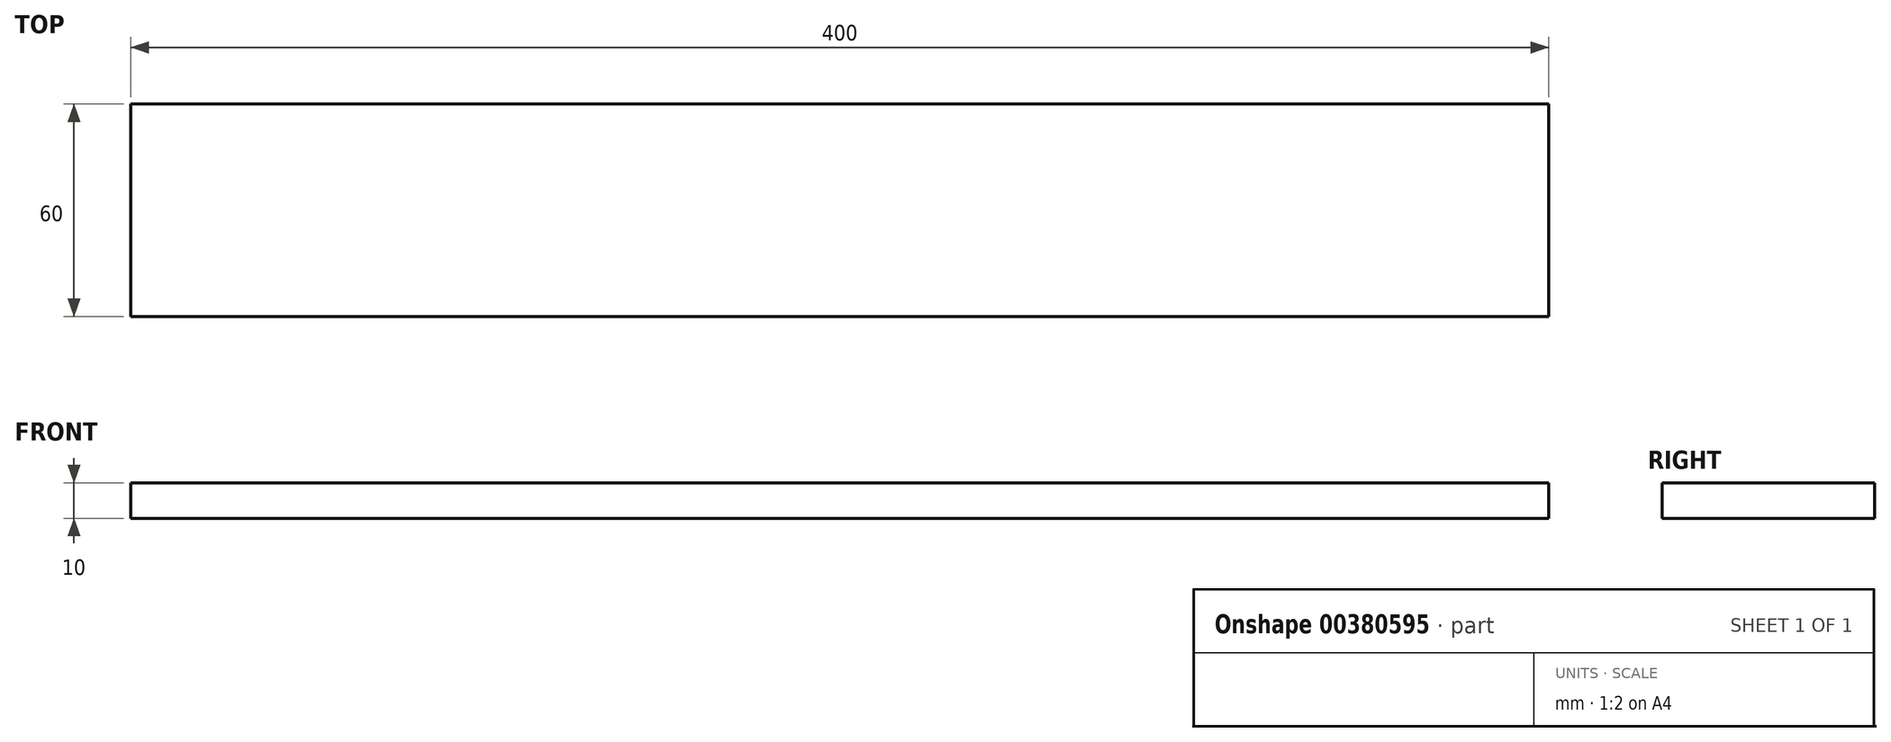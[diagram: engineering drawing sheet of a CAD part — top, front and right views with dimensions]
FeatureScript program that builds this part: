
annotation { "Feature Type Name" : "Feature", "Feature Type Description" : "" }
export const myFeature = defineFeature(function(context is Context, id is Id, definition is map)
    precondition{}
    {
        {
            var Q0;
            Q0=qCreatedBy(makeId("Top.planeOp"),FACE);
            var sketch = newSketch(context, id + "F0", { "sketchPlane" : qUnion([Q0])});
            skLineSegment(sketch, "E0.bottom", {"start": v(200, -30) * mm, "end": v(-200, -30) * mm});
            skLineSegment(sketch, "E0.top", {"start": v(200, 30) * mm, "end": v(-200, 30) * mm});
            skLineSegment(sketch, "E0.left", {"start": v(200, -30) * mm, "end": v(200, 30) * mm});
            skLineSegment(sketch, "E0.right", {"start": v(-200, -30) * mm, "end": v(-200, 30) * mm});
            skPoint(sketch, "E0.middle", {"position": v(0, 0) * mm});
            skSolve(sketch);
        }
        {
            var Q0;
            Q0 = qSketchRegion(id + "F0", true);
            extrude(context, id + "F1", {"entities" : qUnion([Q0]), "depth" : 10 * mm});
        }
    });
